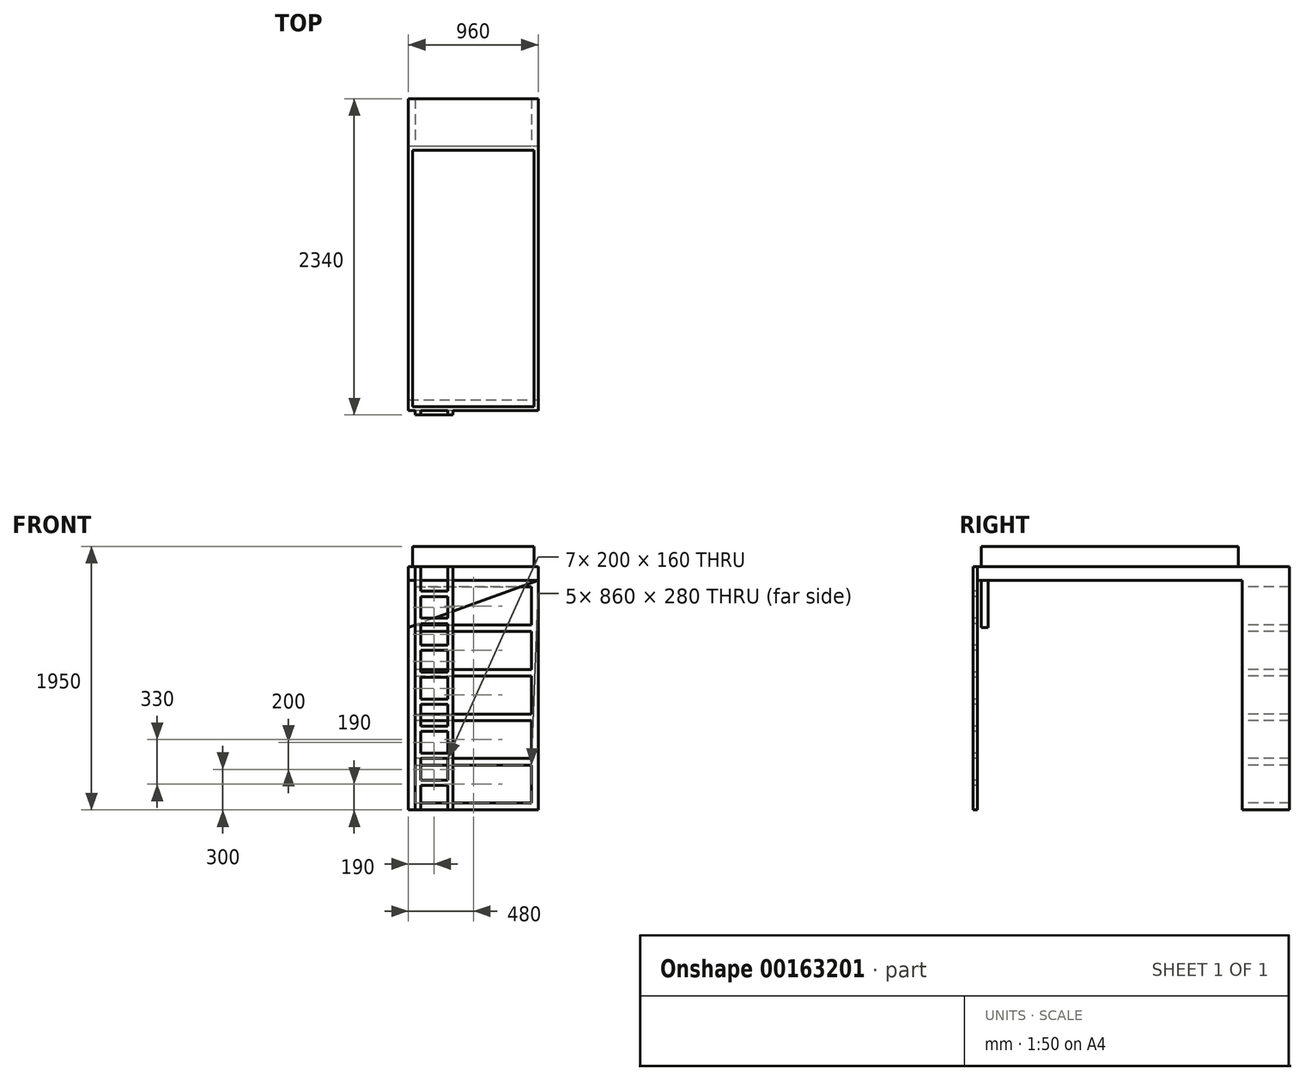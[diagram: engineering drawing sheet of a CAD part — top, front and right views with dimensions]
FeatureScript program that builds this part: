
annotation { "Feature Type Name" : "Feature", "Feature Type Description" : "" }
export const myFeature = defineFeature(function(context is Context, id is Id, definition is map)
    precondition{}
    {
        {
            var Q0;
            Q0=qCreatedBy(makeId("Top.planeOp"),FACE);
            var sketch = newSketch(context, id + "F0", { "sketchPlane" : qUnion([Q0])});
            skLineSegment(sketch, "E0.bottom", {"start": v(-450, 950) * mm, "end": v(450, 950) * mm});
            skLineSegment(sketch, "E0.top", {"start": v(-450, -950) * mm, "end": v(450, -950) * mm});
            skLineSegment(sketch, "E0.left", {"start": v(-450, 950) * mm, "end": v(-450, -950) * mm});
            skLineSegment(sketch, "E0.right", {"start": v(450, 950) * mm, "end": v(450, -950) * mm});
            skPoint(sketch, "E0.middle", {"position": v(0, 0) * mm});
            skSolve(sketch);
        }
        {
            var Q0;
            Q0 = qSketchRegion(id + "F0", true);
            extrude(context, id + "F1", {"entities" : qUnion([Q0]), "depth" : 150 * mm});
        }
        {
            var Q0;
            Q0=makeQuery(id+"F1.opExtrude","CAP_FACE",FACE,{"disambiguationData":[OSD([sQuery(id+"F0.wireOp",EDGE,"E0.bottom"),sQuery(id+"F0.wireOp",EDGE,"E0.top"),sQuery(id+"F0.wireOp",EDGE,"E0.left"),sQuery(id+"F0.wireOp",EDGE,"E0.right")])],"isStart":true});
            var sketch = newSketch(context, id + "F2", { "sketchPlane" : qUnion([Q0])});
            skLineSegment(sketch, "E1.0", {"start": v(-480, -980) * mm, "end": v(480, -980) * mm, "construction": true});
            skLineSegment(sketch, "E1.1", {"start": v(-480, 980) * mm, "end": v(-480, -980) * mm});
            skLineSegment(sketch, "E1.2", {"start": v(480, 980) * mm, "end": v(-480, 980) * mm});
            skLineSegment(sketch, "E1.3", {"start": v(480, -980) * mm, "end": v(480, 980) * mm});
            skLineSegment(sketch, "E2", {"start": v(-480, -980) * mm, "end": v(-480, -1330) * mm});
            skLineSegment(sketch, "E3", {"start": v(-480, -1330) * mm, "end": v(480, -1330) * mm});
            skLineSegment(sketch, "E4", {"start": v(480, -1330) * mm, "end": v(480, -980) * mm});
            skSolve(sketch);
        }
        {
            var Q0;
            Q0 = qSketchRegion(id + "F2", true);
            extrude(context, id + "F3", {"entities" : qUnion([Q0]), "operationType" : NewBodyOperationType.ADD, "depth" : 100 * mm});
        }
        {
            var Q0;
            Q0=makeQuery(id+"F3.opExtrude","CAP_FACE",FACE,{"disambiguationData":[OSD([sQuery(id+"F2.wireOp",EDGE,"E1.1"),sQuery(id+"F2.wireOp",EDGE,"E1.2"),sQuery(id+"F2.wireOp",EDGE,"E1.3"),sQuery(id+"F2.wireOp",EDGE,"E2"),sQuery(id+"F2.wireOp",EDGE,"E3"),sQuery(id+"F2.wireOp",EDGE,"E4")])],"isStart":false});
            var sketch = newSketch(context, id + "F4", { "sketchPlane" : qUnion([Q0])});
            skLineSegment(sketch, "E5.0", {"start": v(-480, -980) * mm, "end": v(480, -980) * mm});
            skLineSegment(sketch, "E6", {"start": v(-480, -980) * mm, "end": v(-480, -1330) * mm});
            skLineSegment(sketch, "E7", {"start": v(-480, -1330) * mm, "end": v(480, -1330) * mm});
            skLineSegment(sketch, "E8", {"start": v(480, -1330) * mm, "end": v(480, -980) * mm});
            skSolve(sketch);
        }
        {
            var Q0;
            Q0 = qSketchRegion(id + "F4", true);
            extrude(context, id + "F5", {"entities" : qUnion([Q0]), "operationType" : NewBodyOperationType.ADD, "depth" : 1700 * mm});
        }
        {
            var Q0;
            Q0=makeQuery(id+"F5.opExtrude","SWEPT_FACE",FACE,{"disambiguationData":[OSD([sQuery(id+"F4.wireOp",EDGE,"E5.0")])]});
            var sketch = newSketch(context, id + "F6", { "sketchPlane" : qUnion([Q0])});
            skLineSegment(sketch, "E9.bottom", {"start": v(-430, -150) * mm, "end": v(430, -150) * mm});
            skLineSegment(sketch, "E9.top", {"start": v(-430, -430) * mm, "end": v(430, -430) * mm});
            skLineSegment(sketch, "E9.left", {"start": v(-430, -150) * mm, "end": v(-430, -430) * mm});
            skLineSegment(sketch, "E9.right", {"start": v(430, -150) * mm, "end": v(430, -430) * mm});
            skLineSegment(sketch, "E10.bottom", {"start": v(430, -480) * mm, "end": v(-430, -480) * mm});
            skLineSegment(sketch, "E10.top", {"start": v(430, -760) * mm, "end": v(-430, -760) * mm});
            skLineSegment(sketch, "E10.left", {"start": v(430, -480) * mm, "end": v(430, -760) * mm});
            skLineSegment(sketch, "E10.right", {"start": v(-430, -480) * mm, "end": v(-430, -760) * mm});
            skLineSegment(sketch, "E11.bottom", {"start": v(-430, -810) * mm, "end": v(430, -810) * mm});
            skLineSegment(sketch, "E11.top", {"start": v(-430, -1090) * mm, "end": v(430, -1090) * mm});
            skLineSegment(sketch, "E11.left", {"start": v(-430, -810) * mm, "end": v(-430, -1090) * mm});
            skLineSegment(sketch, "E11.right", {"start": v(430, -810) * mm, "end": v(430, -1090) * mm});
            skLineSegment(sketch, "E12.bottom", {"start": v(430, -1140) * mm, "end": v(-430, -1140) * mm});
            skLineSegment(sketch, "E12.top", {"start": v(430, -1420) * mm, "end": v(-430, -1420) * mm});
            skLineSegment(sketch, "E12.left", {"start": v(430, -1140) * mm, "end": v(430, -1420) * mm});
            skLineSegment(sketch, "E12.right", {"start": v(-430, -1140) * mm, "end": v(-430, -1420) * mm});
            skLineSegment(sketch, "E13.bottom", {"start": v(-430, -1470) * mm, "end": v(430, -1470) * mm});
            skLineSegment(sketch, "E13.top", {"start": v(-430, -1750) * mm, "end": v(430, -1750) * mm});
            skLineSegment(sketch, "E13.left", {"start": v(-430, -1470) * mm, "end": v(-430, -1750) * mm});
            skLineSegment(sketch, "E13.right", {"start": v(430, -1470) * mm, "end": v(430, -1750) * mm});
            skPoint(sketch, "E14", {"position": v(0, -150) * mm});
            skLineSegment(sketch, "E15", {"start": v(430, -150) * mm, "end": v(430, -100) * mm, "construction": true});
            skLineSegment(sketch, "E16", {"start": v(430, -430) * mm, "end": v(430, -480) * mm, "construction": true});
            skLineSegment(sketch, "E17", {"start": v(430, -760) * mm, "end": v(430, -810) * mm, "construction": true});
            skLineSegment(sketch, "E18", {"start": v(430, -1090) * mm, "end": v(430, -1140) * mm, "construction": true});
            skLineSegment(sketch, "E19", {"start": v(430, -1420) * mm, "end": v(430, -1470) * mm, "construction": true});
            skLineSegment(sketch, "E20", {"start": v(430, -1750) * mm, "end": v(430, -1800) * mm, "construction": true});
            skLineSegment(sketch, "E21", {"start": v(430, -150) * mm, "end": v(480, -150) * mm, "construction": true});
            skSolve(sketch);
        }
        {
            var Q0;
            Q0 = qSketchRegion(id + "F6", true);
            extrude(context, id + "F7", {"entities" : qUnion([Q0]), "operationType" : NewBodyOperationType.REMOVE, "endBound" : BoundingType.UP_TO_NEXT, "oppositeDirection" : true, "depth" : 25 * mm});
        }
        {
            var Q0;
            Q0=makeQuery(id+"F1.opExtrude","SWEPT_FACE",FACE,{"disambiguationData":[OSD([sQuery(id+"F0.wireOp",EDGE,"E0.top")])]});
            var sketch = newSketch(context, id + "F8", { "sketchPlane" : qUnion([Q0])});
            skLineSegment(sketch, "E22", {"start": v(-480, -100) * mm, "end": v(480, -100) * mm});
            skLineSegment(sketch, "E23", {"start": v(480, -100) * mm, "end": v(-480, -449.41) * mm});
            skLineSegment(sketch, "E24", {"start": v(-480, -449.41) * mm, "end": v(-480, -100) * mm});
            skSolve(sketch);
        }
        {
            var Q0;
            Q0 = qSketchRegion(id + "F8", true);
            extrude(context, id + "F9", {"entities" : qUnion([Q0]), "operationType" : NewBodyOperationType.ADD, "oppositeDirection" : true, "depth" : 50 * mm});
        }
        {
            var Q0;
            Q0=makeQuery(id+"F3.opExtrude","SWEPT_FACE",FACE,{"disambiguationData":[OSD([sQuery(id+"F2.wireOp",EDGE,"E1.2")])]});
            var sketch = newSketch(context, id + "F10", { "sketchPlane" : qUnion([Q0])});
            skLineSegment(sketch, "E25.bottom", {"start": v(-430, 0) * mm, "end": v(-390, 0) * mm});
            skLineSegment(sketch, "E25.top", {"start": v(-430, -1800) * mm, "end": v(-390, -1800) * mm});
            skLineSegment(sketch, "E25.left", {"start": v(-430, 0) * mm, "end": v(-430, -1800) * mm});
            skLineSegment(sketch, "E25.right", {"start": v(-390, 0) * mm, "end": v(-390, -1800) * mm});
            skLineSegment(sketch, "E26.bottom", {"start": v(-190, 0) * mm, "end": v(-150, 0) * mm});
            skLineSegment(sketch, "E26.top", {"start": v(-190, -1800) * mm, "end": v(-150, -1800) * mm});
            skLineSegment(sketch, "E26.left", {"start": v(-190, 0) * mm, "end": v(-190, -1800) * mm});
            skLineSegment(sketch, "E26.right", {"start": v(-150, 0) * mm, "end": v(-150, -1800) * mm});
            skSolve(sketch);
        }
        {
            var Q0;
            Q0 = qSketchRegion(id + "F10", true);
            extrude(context, id + "F11", {"entities" : qUnion([Q0]), "operationType" : NewBodyOperationType.ADD, "depth" : 30 * mm});
        }
        {
            var Q0;
            Q0=makeQuery(id+"F11.opExtrude","CAP_FACE",FACE,{"disambiguationData":[OSD([sQuery(id+"F10.wireOp",EDGE,"E25.bottom"),sQuery(id+"F10.wireOp",EDGE,"E25.top"),sQuery(id+"F10.wireOp",EDGE,"E25.left"),sQuery(id+"F10.wireOp",EDGE,"E25.right")])],"isStart":false});
            var sketch = newSketch(context, id + "F12", { "sketchPlane" : qUnion([Q0])});
            skLineSegment(sketch, "E27.bottom", {"start": v(-390, -180) * mm, "end": v(-190, -180) * mm});
            skLineSegment(sketch, "E27.top", {"start": v(-390, -220) * mm, "end": v(-190, -220) * mm});
            skLineSegment(sketch, "E27.left", {"start": v(-390, -180) * mm, "end": v(-390, -220) * mm});
            skLineSegment(sketch, "E27.right", {"start": v(-190, -180) * mm, "end": v(-190, -220) * mm});
            skLineSegment(sketch, "E28.bottom", {"start": v(-390, -380) * mm, "end": v(-190, -380) * mm});
            skLineSegment(sketch, "E28.top", {"start": v(-390, -420) * mm, "end": v(-190, -420) * mm});
            skLineSegment(sketch, "E28.left", {"start": v(-390, -380) * mm, "end": v(-390, -420) * mm});
            skLineSegment(sketch, "E28.right", {"start": v(-190, -380) * mm, "end": v(-190, -420) * mm});
            skLineSegment(sketch, "E29.bottom", {"start": v(-390, -580) * mm, "end": v(-190, -580) * mm});
            skLineSegment(sketch, "E29.top", {"start": v(-390, -620) * mm, "end": v(-190, -620) * mm});
            skLineSegment(sketch, "E29.left", {"start": v(-390, -580) * mm, "end": v(-390, -620) * mm});
            skLineSegment(sketch, "E29.right", {"start": v(-190, -580) * mm, "end": v(-190, -620) * mm});
            skLineSegment(sketch, "E30.bottom", {"start": v(-390, -780) * mm, "end": v(-190, -780) * mm});
            skLineSegment(sketch, "E30.top", {"start": v(-390, -820) * mm, "end": v(-190, -820) * mm});
            skLineSegment(sketch, "E30.left", {"start": v(-390, -780) * mm, "end": v(-390, -820) * mm});
            skLineSegment(sketch, "E30.right", {"start": v(-190, -780) * mm, "end": v(-190, -820) * mm});
            skLineSegment(sketch, "E31.bottom", {"start": v(-390, -980) * mm, "end": v(-190, -980) * mm});
            skLineSegment(sketch, "E31.top", {"start": v(-390, -1020) * mm, "end": v(-190, -1020) * mm});
            skLineSegment(sketch, "E31.left", {"start": v(-390, -980) * mm, "end": v(-390, -1020) * mm});
            skLineSegment(sketch, "E31.right", {"start": v(-190, -980) * mm, "end": v(-190, -1020) * mm});
            skLineSegment(sketch, "E32.bottom", {"start": v(-390, -1180) * mm, "end": v(-190, -1180) * mm});
            skLineSegment(sketch, "E32.top", {"start": v(-390, -1220) * mm, "end": v(-190, -1220) * mm});
            skLineSegment(sketch, "E32.left", {"start": v(-390, -1180) * mm, "end": v(-390, -1220) * mm});
            skLineSegment(sketch, "E32.right", {"start": v(-190, -1180) * mm, "end": v(-190, -1220) * mm});
            skLineSegment(sketch, "E33.bottom", {"start": v(-390, -1380) * mm, "end": v(-190, -1380) * mm});
            skLineSegment(sketch, "E33.top", {"start": v(-390, -1420) * mm, "end": v(-190, -1420) * mm});
            skLineSegment(sketch, "E33.left", {"start": v(-390, -1380) * mm, "end": v(-390, -1420) * mm});
            skLineSegment(sketch, "E33.right", {"start": v(-190, -1380) * mm, "end": v(-190, -1420) * mm});
            skLineSegment(sketch, "E34.bottom", {"start": v(-390, -1580) * mm, "end": v(-190, -1580) * mm});
            skLineSegment(sketch, "E34.top", {"start": v(-390, -1620) * mm, "end": v(-190, -1620) * mm});
            skLineSegment(sketch, "E34.left", {"start": v(-390, -1580) * mm, "end": v(-390, -1620) * mm});
            skLineSegment(sketch, "E34.right", {"start": v(-190, -1580) * mm, "end": v(-190, -1620) * mm});
            skLineSegment(sketch, "E35", {"start": v(-390, -220) * mm, "end": v(-390, -380) * mm, "construction": true});
            skLineSegment(sketch, "E36", {"start": v(-390, -420) * mm, "end": v(-390, -580) * mm, "construction": true});
            skLineSegment(sketch, "E37", {"start": v(-390, -620) * mm, "end": v(-390, -780) * mm, "construction": true});
            skLineSegment(sketch, "E38", {"start": v(-390, -820) * mm, "end": v(-390, -980) * mm, "construction": true});
            skLineSegment(sketch, "E39", {"start": v(-390, -1020) * mm, "end": v(-390, -1180) * mm, "construction": true});
            skLineSegment(sketch, "E40", {"start": v(-390, -1220) * mm, "end": v(-390, -1380) * mm, "construction": true});
            skLineSegment(sketch, "E41", {"start": v(-390, -1420) * mm, "end": v(-390, -1580) * mm, "construction": true});
            skLineSegment(sketch, "E42", {"start": v(-190, -180) * mm, "end": v(-190, 0) * mm, "construction": true});
            skLineSegment(sketch, "E43", {"start": v(-190, -1620) * mm, "end": v(-190, -1800) * mm, "construction": true});
            skSolve(sketch);
        }
        {
            var Q0;
            Q0 = qSketchRegion(id + "F12", true);
            var Q1;
            {var subQ4=sQuery(id+"F2.wireOp",EDGE,"E1.2");Q1=makeQuery(id+"F11.boolean.opBoolean","SPLIT",FACE,{"disambiguationData":[TD([makeQuery(id+"F5.opExtrude","SWEPT_FACE",FACE,{"disambiguationData":[OSD([sQuery(id+"F4.wireOp",EDGE,"E8")])]})])],"derivedFrom":makeQuery(id+"F3.opExtrude","SWEPT_FACE",FACE,{"disambiguationData":[OSD([subQ4])]})});}
            extrude(context, id + "F13", {"entities" : qUnion([Q0]), "operationType" : NewBodyOperationType.ADD, "endBound" : BoundingType.UP_TO_SURFACE, "oppositeDirection" : true, "endBoundEntityFace" : qUnion([Q1]), "depth" : 25 * mm});
        }
    });
